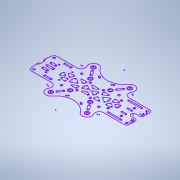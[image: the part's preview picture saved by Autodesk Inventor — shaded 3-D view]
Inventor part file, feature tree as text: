
AUTODESK INVENTOR PART (.ipt)
format: ipt  version: 2020 (Build 240168000, 168)  size: 218,112 bytes
history: native  units: mm
features: sketch x1
ambient origin geometry x8: Origin, YZ Plane, XZ Plane, XY Plane, X Axis, Y Axis, Z Axis, Center Point
feature tree (1):
  sketch  "Sketch1"
